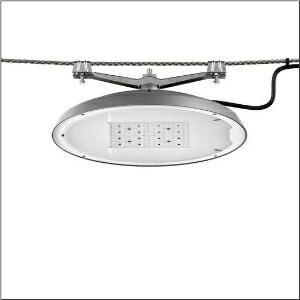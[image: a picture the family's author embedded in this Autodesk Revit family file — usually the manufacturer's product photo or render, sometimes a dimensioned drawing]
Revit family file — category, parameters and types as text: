
# Revit family: dl_r__50_iq_mini___st1_0s_5xa248w31f08me_86a1
name_source: partatom
category: Lighting Fixtures
units: mm (PartAtom-declared; Revit-internal decimal feet)

## family parameters
Cut with Voids When Loaded = No
Host = Face
Light Source = No
Part Type = Normal
Room Calculation Point = No
Round Connector Dimension = Use Diameter
Shared = No

## types (1)
- --- (1 x LED, 15660 lm, 107.8 W, 3000K)
    Apparent Load = 108 VA
    CIE Flux Codes = 37 72 97 100 100
    Color Rendering = 70
    Color Temperature = 3000K
    Default Elevation = 1800 mm
    Description = DL® 50 iQ mini, catenary luminaire, primary light control with lens, of PMMA, primary optical cover: cover, of toughened safety glass, transparent, light distribution: ST1.0s, light emission: direct distribution, primary light characteristic: symmetric, installation type: suspended mounting, LED, High Power LED, rated luminous flux: 15.660lm, luminous efficacy: 145lm/W, light colour: 730, colour temperature: 3000K, control gear: iQ Street-Remote, control: optimised constant luminous flux control (CLO 2.0), Desk-Remote (wireless, voltage-free reading and setting of iQ features in the workshop via application-optimized NFC function/RFID function), Light-Fading, Smart-Wire, Night-Set, Lumen-Switch, Temp-Guard, Auto-Match, Street-Remote, mains connection: 230..240V, AC, 50/60Hz, start of lifetime: 108W, end of service life: 118W, reduction: 47W, luminaire housing, of diecast aluminium, powder-coated, Siteco® metallic grey (DB 702S), diameter: 500mm, height: 115mm, mounting height: 4..12m, protection rating (complete): IP66, insulation class (complete): insulation class II (safety insulation), certification: CE, ENEC, ENEC+, VDE, impact resistance: IK08, permissible operating ambient temperature for outdoor applications: -25..+40°C, standard-compliant lighting for roads and squares, packaging unit: 1 piece

Light Distribution: ST1.0s
    Height = 124 mm  [stored 0.406824 ft]
    Lamp = 1 x LED
    Lamp Light Flux = 15660 lm
    Lamp Power = 107.8 W
    Lamp count = 1
    Length = 500 mm
    Luminous efficacy = 145 lm/W
    Manufacturer = Siteco
    ModVariant = No
    Model = 5XA248W31F08ME
    Number of Poles = 1
    OnlyDefault = Yes
    Power Factor = 1
    Product Name = DL® 50 iQ mini | ST1.0s
    Product group = catenary luminaire
    ProductGroupID = 6300
    Protection Class = Protection class II
    Protection Degree = IP 66
    RLX_Detail_Level = 1
    RLX_Emergency_Light_Flux = 0 lm
    RLX_Emergency_Type = 0
    RLX_Emergency_Type_DB = No
    RlxData = <blob elided: 127157 chars, md5=7200b5f8>
    Socket = socket
    Standby Power = 0 W
    System Light Flux = 15660 lm
    System Power = 108 W
    Type Comments = factory setting: luminous flux: 100 % | dim-lin: 254 | 565 mA
    Type Image = l_1251783.jpg
    URL = http://relux.com
    VarID = @adj_140412
    Voltage = 0 V
    Weight = 0.00 kg
    Width = 0 mm  [stored 0 ft]

note: [stored X ft] marks values corroborated as IEEE doubles in the binary element streams (Revit-internal decimal feet)

## geometry (parser evidence)
native form markers: Blend x4, Sweep x14
no freeform markers — native parametric forms only
